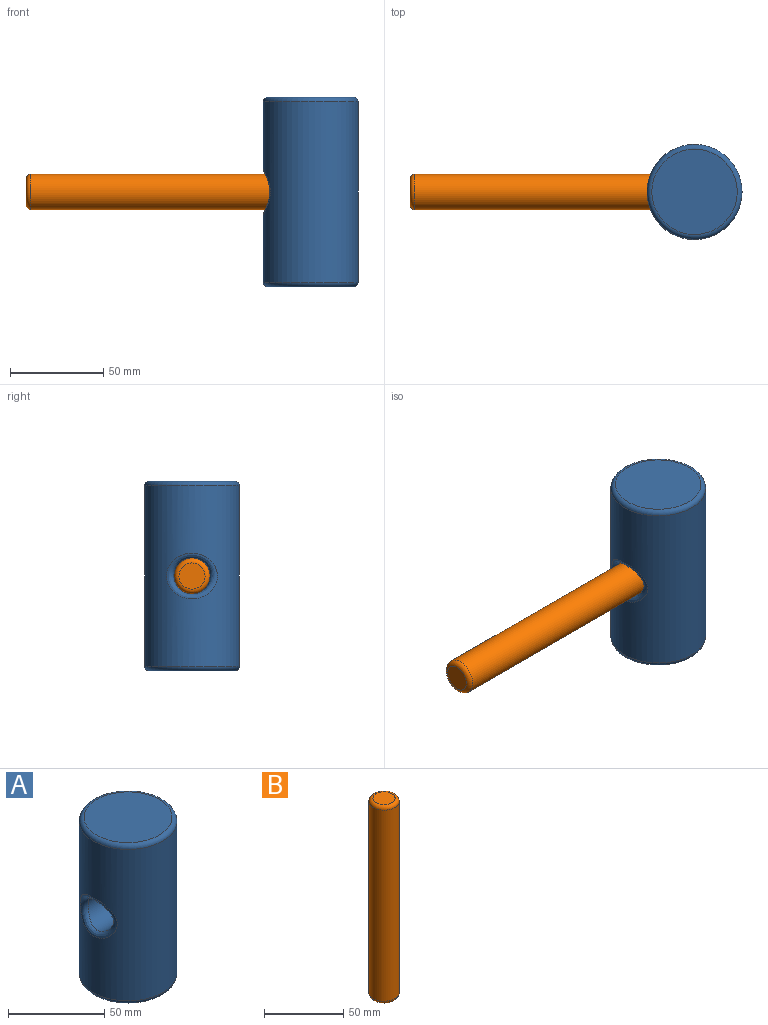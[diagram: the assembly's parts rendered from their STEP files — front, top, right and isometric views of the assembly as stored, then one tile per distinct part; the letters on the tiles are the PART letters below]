
ASSEMBLY  parts=2 mates=1
PART A: 8 faces, bbox 55x55x101.6 mm
  f0: cylinder r=25.4mm len=96.52mm, axis (0,0,-1), area 14860.8mm2, adj f5,f6,f7
  f1: plane 45.72x45.72mm, normal (0,0,1), area 1641.7mm2, adj f7
  f2: plane 45.72x45.72mm, normal (0,0,-1), area 1641.7mm2, adj f6
  f3: cylinder r=9.68mm len=22.86mm, axis (1,0,0), area 1285.4mm2, adj f4,f5
  f4: plane 19.37x19.37mm, normal (-1,0,0), area 294.6mm2, adj f3
  f5: bspline ~27.19x24.47mm, area 327.2mm2, adj f0,f3
  f6: torus R=22.86mm, axis (0,0,1), area 613.6mm2, adj f0,f2
  f7: torus R=22.86mm, axis (0,0,1), area 613.6mm2, adj f0,f1
PART B: 5 faces, bbox 20.6x20.6x152.4 mm
  f0: cylinder r=9.53mm len=147.32mm, axis (0,0,-1), area 8816.7mm2, adj f3,f4
  f1: plane 13.97x13.97mm, normal (0,0,1), area 153.3mm2, adj f4
  f2: plane 13.97x13.97mm, normal (0,0,-1), area 153.3mm2, adj f3
  f3: torus R=6.99mm, axis (0,0,1), area 215.6mm2, adj f0,f2
  f4: torus R=6.99mm, axis (0,0,1), area 215.6mm2, adj f0,f1
PLACE A t=(-34.54,-17.82,3.18)mm
PLACE B rot(axis=(0.71,0,0.71),180deg) t=(-186.94,-17.82,3.71)mm
MATE planar B.f0 <-> A.f3  axis (1,0,0) through (-34.54,-17.82,53.98)mm
